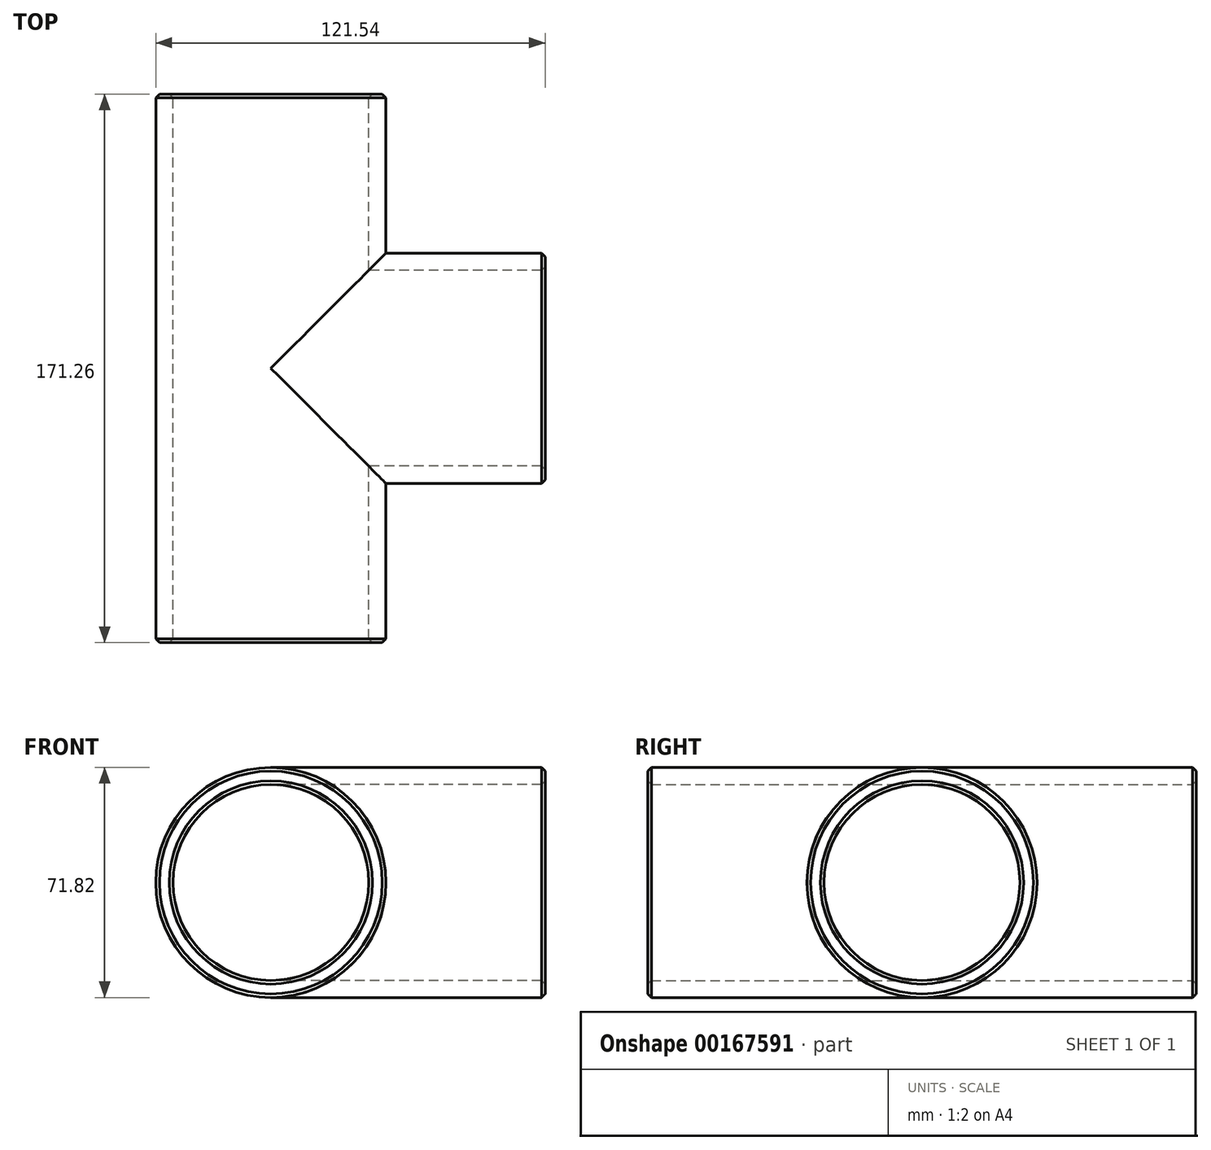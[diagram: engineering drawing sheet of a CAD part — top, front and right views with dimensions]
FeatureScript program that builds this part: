
annotation { "Feature Type Name" : "Feature", "Feature Type Description" : "" }
export const myFeature = defineFeature(function(context is Context, id is Id, definition is map)
    precondition{}
    {
        {
            var Q0;
            Q0=qCreatedBy(makeId("Front.planeOp"),FACE);
            var sketch = newSketch(context, id + "F0", { "sketchPlane" : qUnion([Q0])});
            skCircle(sketch, "E0", {"center": v(0, 0) * mm, "radius": 21.08 * mm});
            skCircle(sketch, "E1.0", {"center": v(0, 0) * mm, "radius": 24.77 * mm});
            skSolve(sketch);
        }
        {
            var Q0;
            Q0=qSketchRegion(id+"F0",true);
            extrude(context, id + "F1", {"entities" : qUnion([Q0]), "endBound" : BoundingType.SYMMETRIC, "depth" : 118.11 * mm});
        }
        {
            var Q0;
            Q0=qCreatedBy(makeId("Right.planeOp"),FACE);
            var sketch = newSketch(context, id + "F2", { "sketchPlane" : qUnion([Q0])});
            skCircle(sketch, "E2", {"center": v(0, 0) * mm, "radius": 21.08 * mm});
            skCircle(sketch, "E3.0", {"center": v(0, 0) * mm, "radius": 24.77 * mm});
            skSolve(sketch);
        }
        {
            var Q0;
            Q0=qSketchRegion(id+"F2",true);
            extrude(context, id + "F3", {"entities" : qUnion([Q0]), "operationType" : NewBodyOperationType.ADD, "depth" : 59.05 * mm});
        }
        {
            var Q0;
            Q0=makeQuery(id+"F2.imprint","IMPRINT",FACE,{"disambiguationData":[TD([[makeQuery(id+"F2.imprint","IMPRINT",EDGE,{"derivedFrom":sQuery(id+"F2.wireOp",EDGE,"E2")}),1.0]])]});
            extrude(context, id + "F4", {"entities" : qUnion([Q0]), "operationType" : NewBodyOperationType.REMOVE, "endBound" : BoundingType.THROUGH_ALL, "depth" : 25.4 * mm});
        }
        {
            var Q0;
            Q0=makeQuery(id+"F0.imprint","IMPRINT",FACE,{"disambiguationData":[TD([[makeQuery(id+"F0.imprint","IMPRINT",EDGE,{"derivedFrom":sQuery(id+"F0.wireOp",EDGE,"E0")}),1.0]])]});
            extrude(context, id + "F5", {"entities" : qUnion([Q0]), "operationType" : NewBodyOperationType.REMOVE, "endBound" : BoundingType.THROUGH_ALL, "depth" : 25.4 * mm, "hasSecondDirection" : true, "secondDirectionBound" : SecondDirectionBoundingType.THROUGH_ALL, "secondDirectionOppositeDirection" : true, "secondDirectionDepth" : 25.4 * mm});
        }
        {
            var Q0;
            Q0=makeQuery(id+"F1.opExtrude","CAP_EDGE",EDGE,{"disambiguationData":[OSD([sQuery(id+"F0.wireOp",EDGE,"E0")])],"isStart":false});
            var Q1;
            Q1=makeQuery(id+"F1.opExtrude","CAP_EDGE",EDGE,{"disambiguationData":[OSD([sQuery(id+"F0.wireOp",EDGE,"E1.0")])],"isStart":false});
            var Q2;
            Q2=makeQuery(id+"F3.opExtrude","CAP_EDGE",EDGE,{"disambiguationData":[OSD([sQuery(id+"F2.wireOp",EDGE,"E3.0")])],"isStart":false});
            var Q3;
            Q3=makeQuery(id+"F3.opExtrude","CAP_EDGE",EDGE,{"disambiguationData":[OSD([sQuery(id+"F2.wireOp",EDGE,"E2")])],"isStart":false});
            var Q4;
            Q4=makeQuery(id+"F1.opExtrude","CAP_EDGE",EDGE,{"disambiguationData":[OSD([sQuery(id+"F0.wireOp",EDGE,"E0")])],"isStart":true});
            var Q5;
            Q5=makeQuery(id+"F1.opExtrude","CAP_EDGE",EDGE,{"disambiguationData":[OSD([sQuery(id+"F0.wireOp",EDGE,"E1.0")])],"isStart":true});
            chamfer(context, id + "F6", {"entities" : qUnion([Q0, Q1, Q2, Q3, Q4, Q5]), "width" : 0.79 * mm, "tangentPropagation" : true});
        }
        {
            var Q0;
            Q0=makeQuery(id+"F1.opExtrude","SWEPT_BODY",BODY,{"disambiguationData":[OSD([sQuery(id+"F0.wireOp",EDGE,"E0"),sQuery(id+"F0.wireOp",EDGE,"E1.0")])]});
            var Q1;
            Q1=qCreatedBy(makeId("Origin.pointOp"),VERTEX);
            transform(context, id + "F7", {"entities" : qUnion([Q0]), "transformType" : TransformType.SCALE_UNIFORMLY, "scale" : 1.45, "scalePoint" : qUnion([Q1]), "makeCopy" : false});
        }
    });
